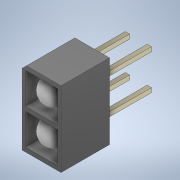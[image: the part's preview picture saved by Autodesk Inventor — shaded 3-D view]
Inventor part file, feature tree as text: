
AUTODESK INVENTOR PART (.ipt)
format: ipt  version: 2022 (Build 260153000, 153)  size: 187,392 bytes
history: native  units: mm
features: extrude x4, other x1, sketch x1, fillet x1
ambient origin geometry x8: Origin, YZ Plane, XZ Plane, XY Plane, X Axis, Y Axis, Z Axis, Center Point
bodies: Body1 (feature_tree)
feature tree (7):
  other  "ソリッド1"
  sketch  "スケッチ1"
  extrude  "押し出し1"  Depth=4.5mm
  extrude  "押し出し2"  Depth=8.7mm
  fillet  "フィレット1"  Radius=4.1mm
  extrude  "押し出し3"  Depth=3.7mm
  extrude  "押し出し4"  Depth=3.6mm
